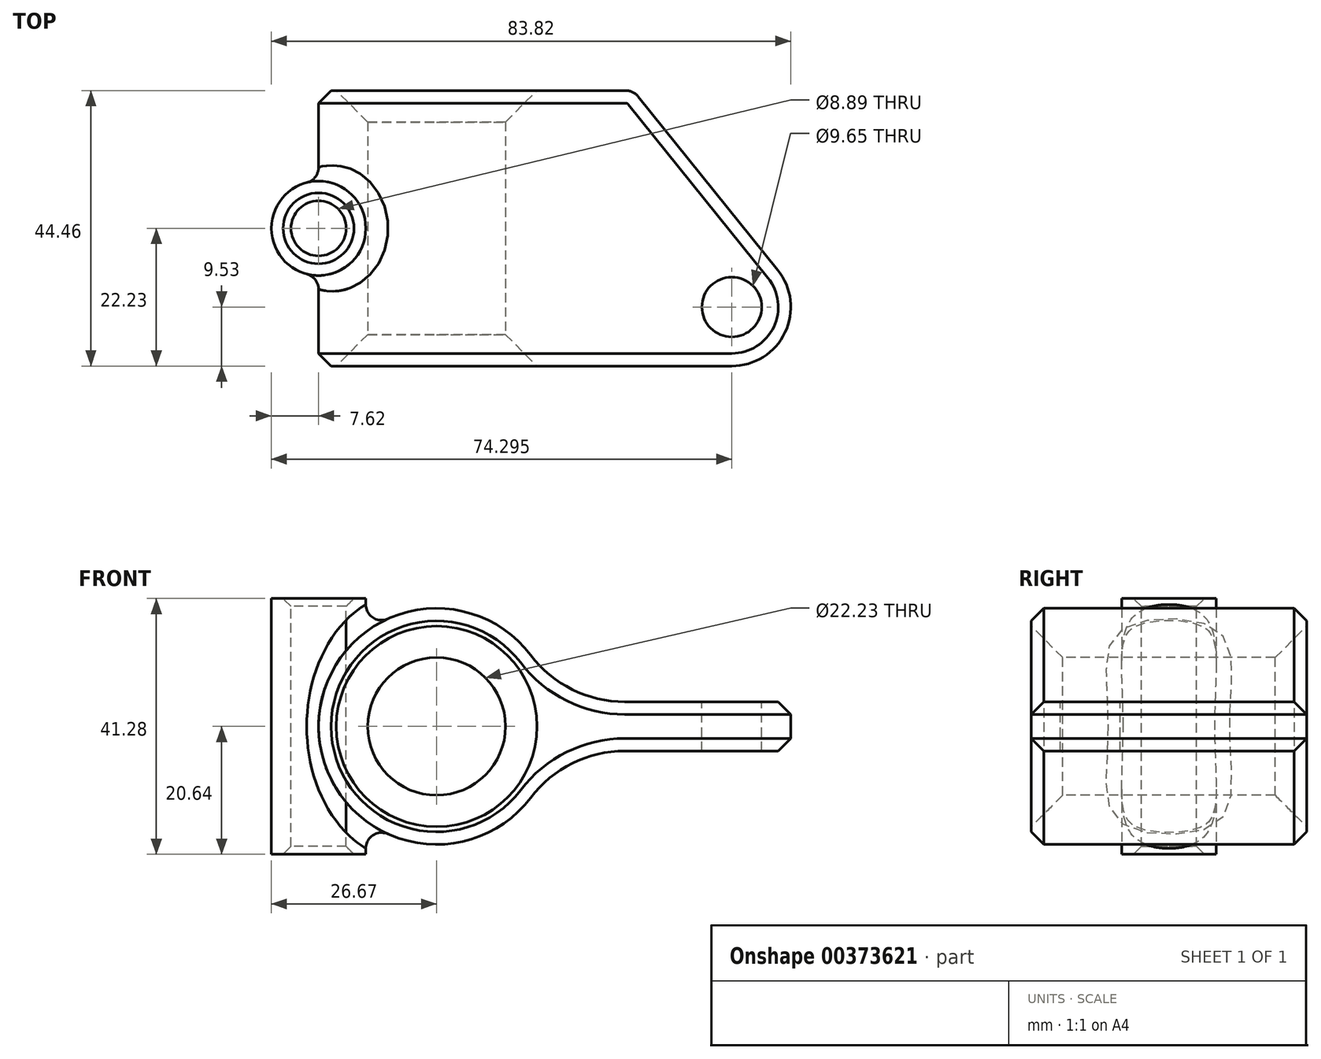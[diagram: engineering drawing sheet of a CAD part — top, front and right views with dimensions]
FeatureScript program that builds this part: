
annotation { "Feature Type Name" : "Feature", "Feature Type Description" : "" }
export const myFeature = defineFeature(function(context is Context, id is Id, definition is map)
    precondition{}
    {
        {
            var Q0;
            Q0=qCreatedBy(makeId("Front.planeOp"),FACE);
            var sketch = newSketch(context, id + "F0", { "sketchPlane" : qUnion([Q0])});
            skCircle(sketch, "E0", {"center": v(0, 0) * mm, "radius": 19.05 * mm});
            skSolve(sketch);
        }
        {
            var Q0;
            Q0=makeQuery(id+"F0.imprint","IMPRINT",FACE,{"disambiguationData":[TD([[makeQuery(id+"F0.imprint","IMPRINT",EDGE,{"derivedFrom":sQuery(id+"F0.wireOp",EDGE,"E0")}),1.0]])]});
            extrude(context, id + "F1", {"entities" : qUnion([Q0]), "depth" : 44.45 * mm, "symmetric" : true});
        }
        {
            var Q0;
            Q0=qCreatedBy(makeId("Top.planeOp"),FACE);
            var sketch = newSketch(context, id + "F2", { "sketchPlane" : qUnion([Q0])});
            skLineSegment(sketch, "E1.0", {"start": v(19.05, -22.23) * mm, "end": v(-19.05, -22.23) * mm});
            skLineSegment(sketch, "E1.1", {"start": v(19.05, 22.23) * mm, "end": v(-19.05, 22.23) * mm});
            skCircle(sketch, "E2", {"center": v(-19.05, 0) * mm, "radius": 7.62 * mm});
            skSolve(sketch);
        }
        {
            var Q0;
            Q0=makeQuery(id+"F2.imprint","IMPRINT",FACE,{"disambiguationData":[TD([[makeQuery(id+"F2.imprint","IMPRINT",EDGE,{"derivedFrom":sQuery(id+"F2.wireOp",EDGE,"E2")}),1.0]])]});
            extrude(context, id + "F3", {"entities" : qUnion([Q0]), "operationType" : NewBodyOperationType.ADD, "depth" : 41.27 * mm, "symmetric" : true});
        }
        {
            var Q0;
            Q0=qCreatedBy(makeId("Top.planeOp"),FACE);
            var sketch = newSketch(context, id + "F4", { "sketchPlane" : qUnion([Q0])});
            skLineSegment(sketch, "E3.0", {"start": v(19.05, 22.23) * mm, "end": v(-19.05, 22.23) * mm});
            skLineSegment(sketch, "E3.1", {"start": v(19.05, -22.23) * mm, "end": v(-19.05, -22.23) * mm});
            skLineSegment(sketch, "E4", {"start": v(0, -22.23) * mm, "end": v(0, 22.23) * mm});
            skLineSegment(sketch, "E5", {"start": v(0, 22.23) * mm, "end": v(31.75, 22.23) * mm});
            skLineSegment(sketch, "E6", {"start": v(31.75, 22.23) * mm, "end": v(55.05, -6.73) * mm});
            skLineSegment(sketch, "E7", {"start": v(19.05, -22.23) * mm, "end": v(47.63, -22.23) * mm});
            skArc(sketch, "E8", {"start": v(47.63, -22.23) * mm, "mid": v(56.22, -16.81) * mm, "end": v(55.05, -6.73) * mm});
            skSolve(sketch);
        }
        {
            var Q0;
            {var subQ3=sQuery(id+"F4.wireOp",EDGE,"E4");Q0=makeQuery(id+"F4.imprint","IMPRINT",FACE,{"disambiguationData":[TD([[makeQuery(id+"F4.imprint","IMPRINT",EDGE,{"derivedFrom":subQ3}),-1.0]])]});}
            extrude(context, id + "F5", {"entities" : qUnion([Q0]), "operationType" : NewBodyOperationType.ADD, "depth" : 7.94 * mm, "symmetric" : true});
        }
        {
            var Q0;
            Q0=makeQuery(id+"F3.opExtrude","CAP_FACE",FACE,{"disambiguationData":[OSD([sQuery(id+"F2.wireOp",EDGE,"E2")])],"isStart":false});
            var sketch = newSketch(context, id + "F6", { "sketchPlane" : qUnion([Q0])});
            skCircle(sketch, "E9.0", {"center": v(-19.05, 0) * mm, "radius": 4.44 * mm});
            skSolve(sketch);
        }
        {
            var Q0;
            Q0=makeQuery(id+"F6.imprint","IMPRINT",FACE,{"disambiguationData":[TD([[makeQuery(id+"F6.imprint","IMPRINT",EDGE,{"derivedFrom":sQuery(id+"F6.wireOp",EDGE,"E9.0")}),1.0]])]});
            extrude(context, id + "F7", {"entities" : qUnion([Q0]), "operationType" : NewBodyOperationType.REMOVE, "endBound" : BoundingType.THROUGH_ALL, "oppositeDirection" : true, "depth" : 25.4 * mm});
        }
        {
            var Q0;
            Q0=makeQuery(id+"F5.boolean.opBoolean","MERGE",FACE,{"derivedFrom":[makeQuery(id+"F1.opExtrude","CAP_FACE",FACE,{"disambiguationData":[OSD([sQuery(id+"F0.wireOp",EDGE,"E0")])],"isStart":false}),makeQuery(id+"F5.opExtrude","SWEPT_FACE",FACE,{"disambiguationData":[OSD([sQuery(id+"F4.wireOp",EDGE,"E3.1")])]})]});
            var sketch = newSketch(context, id + "F8", { "sketchPlane" : qUnion([Q0])});
            skCircle(sketch, "E10", {"center": v(0, 0) * mm, "radius": 11.11 * mm});
            skSolve(sketch);
        }
        {
            var Q0;
            Q0=makeQuery(id+"F8.imprint","IMPRINT",FACE,{"disambiguationData":[TD([[makeQuery(id+"F8.imprint","IMPRINT",EDGE,{"derivedFrom":sQuery(id+"F8.wireOp",EDGE,"E10")}),1.0]])]});
            extrude(context, id + "F9", {"entities" : qUnion([Q0]), "operationType" : NewBodyOperationType.REMOVE, "endBound" : BoundingType.THROUGH_ALL, "oppositeDirection" : true, "depth" : 25.4 * mm});
        }
        {
            var Q0;
            Q0=makeQuery(id+"F5.opExtrude","CAP_FACE",FACE,{"disambiguationData":[OSD([sQuery(id+"F4.wireOp",EDGE,"E3.1"),sQuery(id+"F4.wireOp",EDGE,"E4"),sQuery(id+"F4.wireOp",EDGE,"E5"),sQuery(id+"F4.wireOp",EDGE,"E6"),sQuery(id+"F4.wireOp",EDGE,"E8")])],"isStart":false});
            var sketch = newSketch(context, id + "F10", { "sketchPlane" : qUnion([Q0])});
            skCircle(sketch, "E11", {"center": v(47.63, -12.7) * mm, "radius": 4.83 * mm});
            skSolve(sketch);
        }
        {
            var Q0;
            Q0=makeQuery(id+"F10.imprint","IMPRINT",FACE,{"disambiguationData":[TD([[makeQuery(id+"F10.imprint","IMPRINT",EDGE,{"derivedFrom":sQuery(id+"F10.wireOp",EDGE,"E11")}),1.0]])]});
            extrude(context, id + "F11", {"entities" : qUnion([Q0]), "operationType" : NewBodyOperationType.ADD, "depth" : 25.4 * mm});
        }
        {
            var Q0;
            Q0=makeQuery(id+"F11.opExtrude","CAP_FACE",FACE,{"disambiguationData":[OSD([sQuery(id+"F10.wireOp",EDGE,"E11")])],"isStart":false});
            extrude(context, id + "F12", {"entities" : qUnion([Q0]), "operationType" : NewBodyOperationType.REMOVE, "endBound" : BoundingType.THROUGH_ALL, "oppositeDirection" : true, "depth" : 25.4 * mm});
        }
        {
            var Q0;
            Q0=makeQuery(id+"F5.boolean.opBoolean","INTERSECT",EDGE,{"derivedFrom":[makeQuery(id+"F1.opExtrude","SWEPT_FACE",FACE,{"disambiguationData":[OSD([sQuery(id+"F0.wireOp",EDGE,"E0")])]}),makeQuery(id+"F5.opExtrude","CAP_FACE",FACE,{"disambiguationData":[OSD([sQuery(id+"F4.wireOp",EDGE,"E3.1"),sQuery(id+"F4.wireOp",EDGE,"E4"),sQuery(id+"F4.wireOp",EDGE,"E5"),sQuery(id+"F4.wireOp",EDGE,"E6"),sQuery(id+"F4.wireOp",EDGE,"E8")])],"isStart":false})]});
            var Q1;
            Q1=makeQuery(id+"F5.boolean.opBoolean","INTERSECT",EDGE,{"derivedFrom":[makeQuery(id+"F1.opExtrude","SWEPT_FACE",FACE,{"disambiguationData":[OSD([sQuery(id+"F0.wireOp",EDGE,"E0")])]}),makeQuery(id+"F5.opExtrude","CAP_FACE",FACE,{"disambiguationData":[OSD([sQuery(id+"F4.wireOp",EDGE,"E3.1"),sQuery(id+"F4.wireOp",EDGE,"E4"),sQuery(id+"F4.wireOp",EDGE,"E5"),sQuery(id+"F4.wireOp",EDGE,"E6"),sQuery(id+"F4.wireOp",EDGE,"E8")])],"isStart":true})]});
            fillet(context, id + "F13", {"entities" : qUnion([Q0, Q1]), "radius" : 19.05 * mm, "tangentPropagation" : true, "allowEdgeOverflow" : false});
        }
        {
            var Q0;
            Q0=makeQuery(id+"F5.opExtrude","SWEPT_EDGE",EDGE,{"disambiguationData":[OSD([sQuery(id+"F4.wireOp",EDGE,"E5"),sQuery(id+"F4.wireOp",EDGE,"E6")])]});
            var Q1;
            Q1=makeQuery(id+"F3.boolean.opBoolean","INTERSECT",EDGE,{"derivedFrom":[makeQuery(id+"F1.opExtrude","SWEPT_FACE",FACE,{"disambiguationData":[OSD([sQuery(id+"F0.wireOp",EDGE,"E0")])]}),makeQuery(id+"F3.opExtrude","SWEPT_FACE",FACE,{"disambiguationData":[OSD([sQuery(id+"F2.wireOp",EDGE,"E2")])]})]});
            fillet(context, id + "F14", {"entities" : qUnion([Q0, Q1]), "radius" : 2.54 * mm, "tangentPropagation" : true, "allowEdgeOverflow" : false});
        }
        {
            var Q0;
            Q0=makeQuery(id+"F1.opExtrude","CAP_EDGE",EDGE,{"disambiguationData":[OSD([sQuery(id+"F0.wireOp",EDGE,"E0")])],"isStart":false});
            chamfer(context, id + "F15", {"entities" : qUnion([Q0]), "width" : 2.03 * mm, "tangentPropagation" : true});
        }
        {
            var Q0;
            Q0=makeQuery(id+"F9.boolean.opBoolean","COPY",FACE,{"derivedFrom":makeQuery(id+"F9.opExtrude","SWEPT_FACE",FACE,{"disambiguationData":[OSD([sQuery(id+"F8.wireOp",EDGE,"E10")])]})});
            chamfer(context, id + "F16", {"entities" : qUnion([Q0]), "width" : 5.08 * mm, "tangentPropagation" : true});
        }
        {
            var Q0;
            Q0=makeQuery(id+"F11.opExtrude","CAP_EDGE",EDGE,{"disambiguationData":[OSD([sQuery(id+"F10.wireOp",EDGE,"E11")])],"isStart":true});
            var Q1;
            Q1=makeQuery(id+"F7.boolean.opBoolean","COPY",FACE,{"derivedFrom":makeQuery(id+"F7.opExtrude","SWEPT_FACE",FACE,{"disambiguationData":[OSD([sQuery(id+"F6.wireOp",EDGE,"E9.0")])]})});
            chamfer(context, id + "F17", {"entities" : qUnion([Q0, Q1]), "width" : 1.27 * mm, "tangentPropagation" : true});
        }
    });
